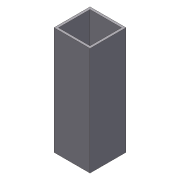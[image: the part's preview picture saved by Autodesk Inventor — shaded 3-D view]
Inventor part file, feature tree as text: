
AUTODESK INVENTOR PART (.ipt)
format: ipt  version: 2012 (Build 160160000, 160)  size: 71,680 bytes
history: native  units: in
note: dims shown in document units (in); Inventor stores cm internally (conversion verified against a paired STEP export)
features: extrude x1, shell x1, sketch x1
ambient origin geometry x8: Origin, YZ Plane, XZ Plane, XY Plane, X Axis, Y Axis, Z Axis, Center Point
bodies: Solid1 (feature_tree)
feature tree (3):
  extrude  "Extrusion1"  Depth=3.0in
  shell  "Shell1"  Thickness=1.0in
  sketch  "Sketch1"  dims[d0=1.0in d1=3.0in d2=1.0in d3=0.0in d4=0.0625in]
